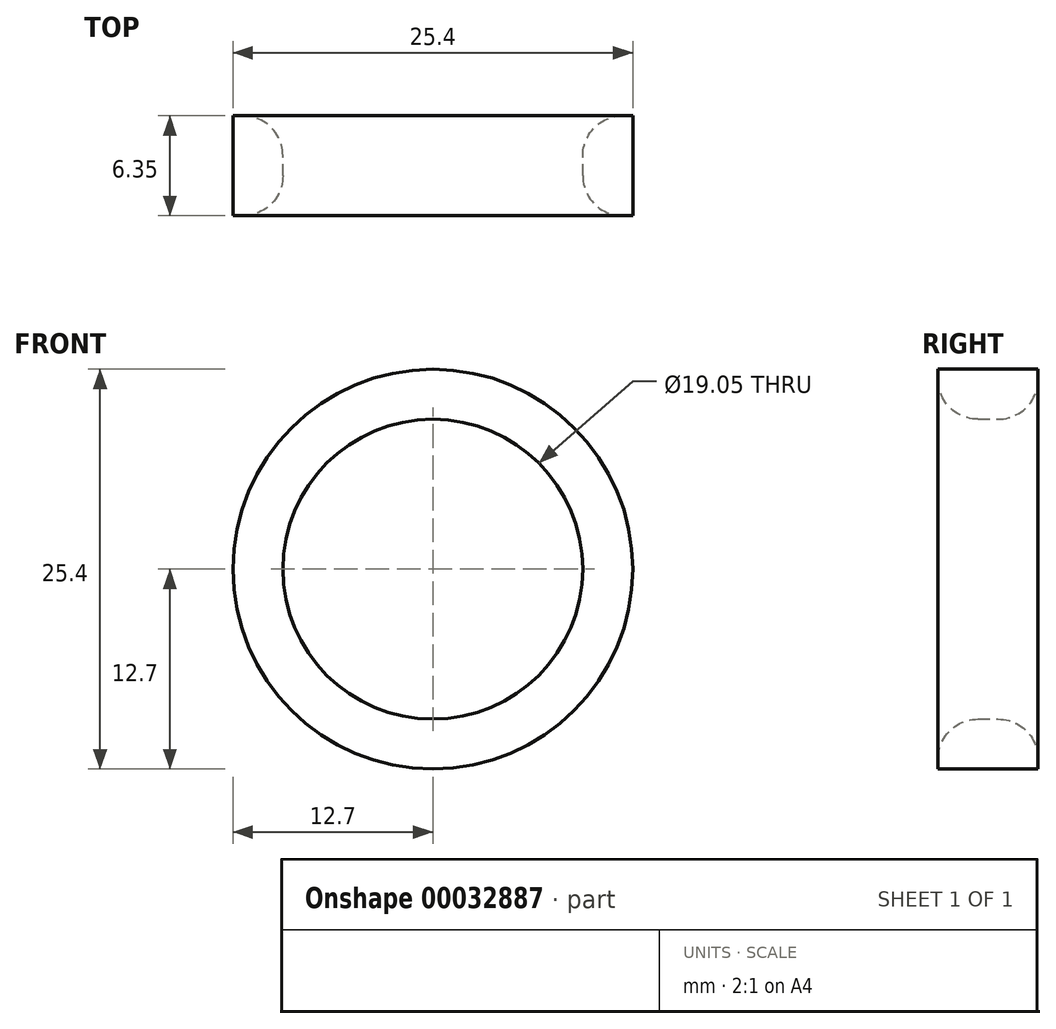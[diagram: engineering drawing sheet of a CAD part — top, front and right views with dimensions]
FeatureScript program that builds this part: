
annotation { "Feature Type Name" : "Feature", "Feature Type Description" : "" }
export const myFeature = defineFeature(function(context is Context, id is Id, definition is map)
    precondition{}
    {
        {
            var Q0;
            Q0=qCreatedBy(makeId("Front.planeOp"),FACE);
            var sketch = newSketch(context, id + "F0", { "sketchPlane" : qUnion([Q0])});
            skCircle(sketch, "E0", {"center": v(0, 0) * mm, "radius": 9.53 * mm});
            skCircle(sketch, "E1", {"center": v(0, 0) * mm, "radius": 12.7 * mm});
            skSolve(sketch);
        }
        {
            var Q0;
            Q0 = qSketchRegion(id + "F0", true);
            extrude(context, id + "F1", {"entities" : qUnion([Q0]), "depth" : 6.35 * mm});
        }
        {
            var Q0;
            Q0=makeQuery(id+"F1.opExtrude","CAP_EDGE",EDGE,{"disambiguationData":[OSD([sQuery(id+"F0.wireOp",EDGE,"E0")])],"isStart":false});
            var Q1;
            Q1=makeQuery(id+"F1.opExtrude","CAP_EDGE",EDGE,{"disambiguationData":[OSD([sQuery(id+"F0.wireOp",EDGE,"E0")])],"isStart":true});
            fillet(context, id + "F2", {"entities" : qUnion([Q0, Q1]), "radius" : 2.54 * mm, "tangentPropagation" : true, "allowEdgeOverflow" : false});
        }
    });
